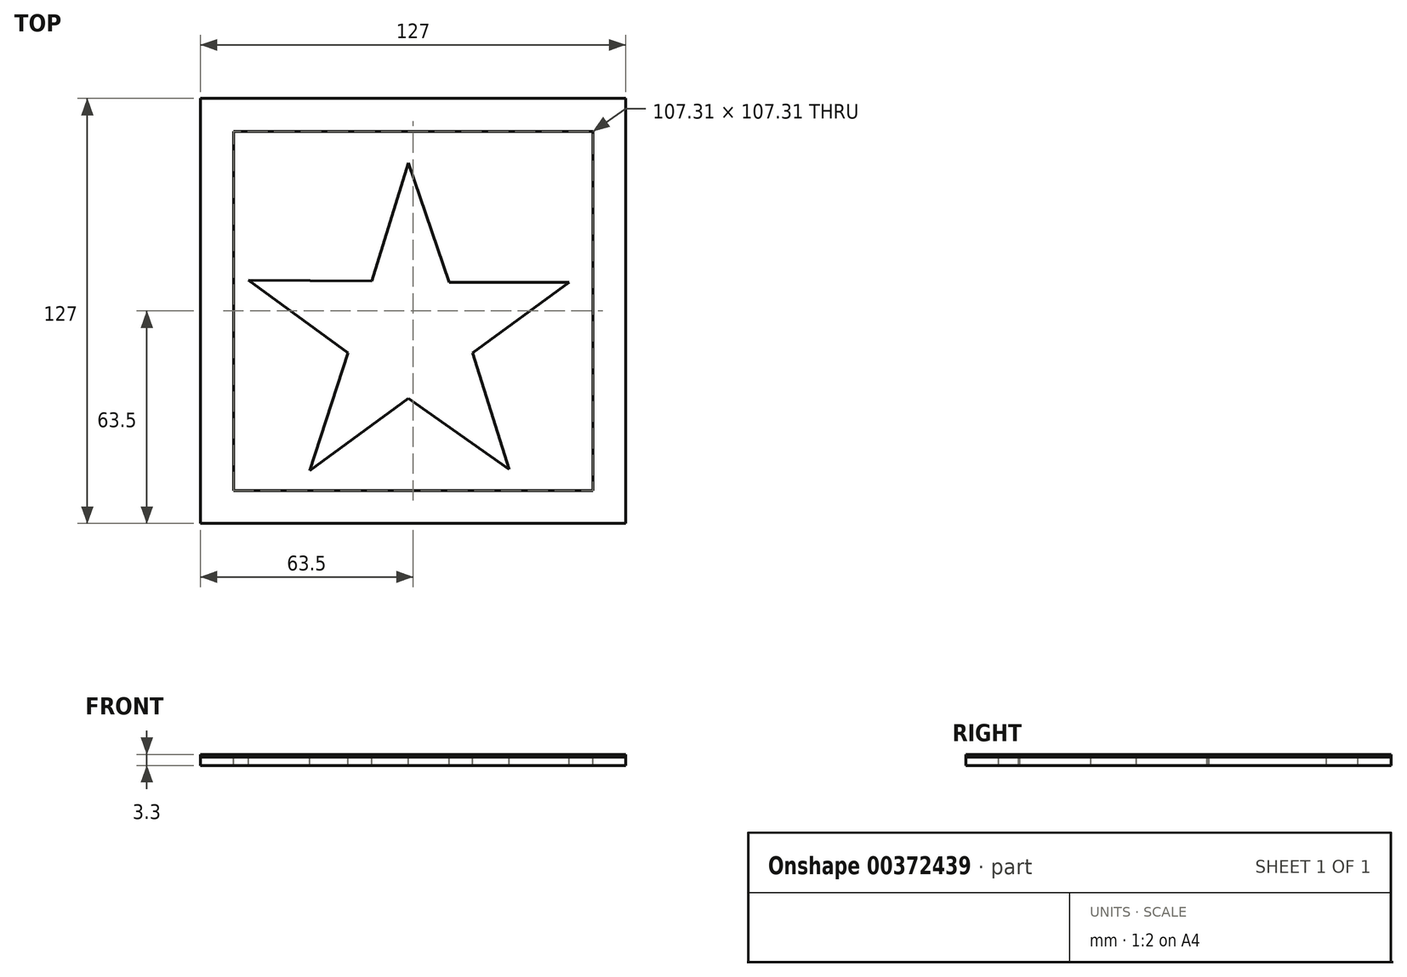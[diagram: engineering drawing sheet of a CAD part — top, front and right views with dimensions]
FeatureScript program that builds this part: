
annotation { "Feature Type Name" : "Feature", "Feature Type Description" : "" }
export const myFeature = defineFeature(function(context is Context, id is Id, definition is map)
    precondition{}
    {
        {
            var Q0;
            Q0=qCreatedBy(makeId("Top.planeOp"),FACE);
            var sketch = newSketch(context, id + "F0", { "sketchPlane" : qUnion([Q0])});
            skLineSegment(sketch, "E0.bottom", {"start": v(10.59, 9.95) * mm, "end": v(61.39, 9.95) * mm});
            skLineSegment(sketch, "E0.top", {"start": v(10.59, 60.75) * mm, "end": v(61.39, 60.75) * mm});
            skLineSegment(sketch, "E0.left", {"start": v(10.59, 9.95) * mm, "end": v(10.59, 60.75) * mm});
            skLineSegment(sketch, "E0.right", {"start": v(61.39, 9.95) * mm, "end": v(61.39, 60.75) * mm});
            skLineSegment(sketch, "E1", {"start": v(31.03, 38.9) * mm, "end": v(35.45, 53.05) * mm});
            skLineSegment(sketch, "E2", {"start": v(35.45, 53.05) * mm, "end": v(40.28, 38.76) * mm});
            skLineSegment(sketch, "E3", {"start": v(40.28, 38.76) * mm, "end": v(54.64, 38.76) * mm});
            skLineSegment(sketch, "E4", {"start": v(54.64, 38.76) * mm, "end": v(43.11, 30.34) * mm});
            skLineSegment(sketch, "E5", {"start": v(43.11, 30.34) * mm, "end": v(47.46, 16.4) * mm});
            skLineSegment(sketch, "E6", {"start": v(47.46, 16.4) * mm, "end": v(35.45, 24.89) * mm});
            skLineSegment(sketch, "E7", {"start": v(35.45, 24.89) * mm, "end": v(23.65, 16.26) * mm});
            skLineSegment(sketch, "E8", {"start": v(23.65, 16.26) * mm, "end": v(28.2, 30.34) * mm});
            skLineSegment(sketch, "E9", {"start": v(28.2, 30.34) * mm, "end": v(16.33, 39.03) * mm});
            skLineSegment(sketch, "E10", {"start": v(16.33, 39.03) * mm, "end": v(31.03, 38.9) * mm});
            skLineSegment(sketch, "E11.bottom", {"start": v(14.53, 13.89) * mm, "end": v(57.45, 13.89) * mm});
            skLineSegment(sketch, "E11.top", {"start": v(14.53, 56.81) * mm, "end": v(57.45, 56.81) * mm});
            skLineSegment(sketch, "E11.left", {"start": v(14.53, 13.89) * mm, "end": v(14.53, 56.81) * mm});
            skLineSegment(sketch, "E11.right", {"start": v(57.45, 13.89) * mm, "end": v(57.45, 56.81) * mm});
            skLineSegment(sketch, "E12", {"start": v(35.45, 53.05) * mm, "end": v(35.45, 60.75) * mm, "construction": true});
            skSolve(sketch);
        }
        {
            var Q0;
            Q0=makeQuery(id+"F0.imprint","IMPRINT",FACE,{"disambiguationData":[TD([[makeQuery(id+"F0.imprint","IMPRINT",EDGE,{"derivedFrom":sQuery(id+"F0.wireOp",EDGE,"E1")}),-1.0]])]});
            var Q1;
            Q1=makeQuery(id+"F0.imprint","IMPRINT",FACE,{"disambiguationData":[TD([[makeQuery(id+"F0.imprint","IMPRINT",EDGE,{"derivedFrom":sQuery(id+"F0.wireOp",EDGE,"E0.bottom")}),1.0]])]});
            extrude(context, id + "F1", {"entities" : qUnion([Q0, Q1]), "oppositeDirection" : true, "depth" : 1.32 * mm});
        }
        {
            var Q0;
            Q0=makeQuery(id+"F1.opExtrude","SWEPT_BODY",BODY,{"disambiguationData":[OSD([sQuery(id+"F0.wireOp",EDGE,"E1"),sQuery(id+"F0.wireOp",EDGE,"E2"),sQuery(id+"F0.wireOp",EDGE,"E3"),sQuery(id+"F0.wireOp",EDGE,"E4"),sQuery(id+"F0.wireOp",EDGE,"E5"),sQuery(id+"F0.wireOp",EDGE,"E6"),sQuery(id+"F0.wireOp",EDGE,"E7"),sQuery(id+"F0.wireOp",EDGE,"E8"),sQuery(id+"F0.wireOp",EDGE,"E9"),sQuery(id+"F0.wireOp",EDGE,"E10")])]});
            var Q1;
            Q1=makeQuery(id+"F1.opExtrude","SWEPT_BODY",BODY,{"disambiguationData":[OSD([sQuery(id+"F0.wireOp",EDGE,"E0.bottom"),sQuery(id+"F0.wireOp",EDGE,"E0.top"),sQuery(id+"F0.wireOp",EDGE,"E0.left"),sQuery(id+"F0.wireOp",EDGE,"E0.right"),sQuery(id+"F0.wireOp",EDGE,"E11.bottom"),sQuery(id+"F0.wireOp",EDGE,"E11.top"),sQuery(id+"F0.wireOp",EDGE,"E11.left"),sQuery(id+"F0.wireOp",EDGE,"E11.right")])]});
            var Q2;
            Q2=qCreatedBy(makeId("Origin.pointOp"),VERTEX);
            transform(context, id + "F2", {"entities" : qUnion([Q0, Q1]), "transformType" : TransformType.SCALE_UNIFORMLY, "scale" : 2.5, "scalePoint" : qUnion([Q2]), "makeCopy" : false});
        }
        {
            var Q0;
            Q0=makeQuery(id+"F1.opExtrude","SWEPT_BODY",BODY,{"disambiguationData":[OSD([sQuery(id+"F0.wireOp",EDGE,"E1"),sQuery(id+"F0.wireOp",EDGE,"E2"),sQuery(id+"F0.wireOp",EDGE,"E3"),sQuery(id+"F0.wireOp",EDGE,"E4"),sQuery(id+"F0.wireOp",EDGE,"E5"),sQuery(id+"F0.wireOp",EDGE,"E6"),sQuery(id+"F0.wireOp",EDGE,"E7"),sQuery(id+"F0.wireOp",EDGE,"E8"),sQuery(id+"F0.wireOp",EDGE,"E9"),sQuery(id+"F0.wireOp",EDGE,"E10")])]});
            var Q1;
            Q1=makeQuery(id+"F1.opExtrude","SWEPT_BODY",BODY,{"disambiguationData":[OSD([sQuery(id+"F0.wireOp",EDGE,"E0.bottom"),sQuery(id+"F0.wireOp",EDGE,"E0.top"),sQuery(id+"F0.wireOp",EDGE,"E0.left"),sQuery(id+"F0.wireOp",EDGE,"E0.right"),sQuery(id+"F0.wireOp",EDGE,"E11.bottom"),sQuery(id+"F0.wireOp",EDGE,"E11.top"),sQuery(id+"F0.wireOp",EDGE,"E11.left"),sQuery(id+"F0.wireOp",EDGE,"E11.right")])]});
            var Q2;
            Q2=makeQuery(id+"F1.opExtrude","CAP_VERTEX",VERTEX,{"disambiguationData":[OSD([sQuery(id+"F0.wireOp",EDGE,"E0.bottom"),sQuery(id+"F0.wireOp",EDGE,"E0.left")])],"isStart":false});
            var Q3;
            Q3=qCreatedBy(makeId("Origin.pointOp"),VERTEX);
            transform(context, id + "F3", {"entities" : qUnion([Q0, Q1]), "transformType" : TransformType.TRANSLATION_ENTITY, "oppositeDirectionEntity" : false, "transformLine" : qUnion([Q2, Q3]), "makeCopy" : false});
        }
        {
            var Q0;
            Q0=qCreatedBy(makeId("Top.planeOp"),FACE);
            var sketch = newSketch(context, id + "F4", { "sketchPlane" : qUnion([Q0])});
            skLineSegment(sketch, "E13.bottom", {"start": v(0, 0) * mm, "end": v(127, 0) * mm});
            skLineSegment(sketch, "E13.top", {"start": v(0, 127) * mm, "end": v(127, 127) * mm});
            skLineSegment(sketch, "E13.left", {"start": v(0, 0) * mm, "end": v(0, 127) * mm});
            skLineSegment(sketch, "E13.right", {"start": v(127, 0) * mm, "end": v(127, 127) * mm});
            skSolve(sketch);
        }
        {
            var Q0;
            Q0 = qSketchRegion(id + "F4", true);
            extrude(context, id + "F5", {"entities" : qUnion([Q0]), "depth" : 2.54 * mm});
        }
    });
